# Revit family: Emergency_Equipment-Haws_Corporation-Laboratory_Combination_Unit_8356WCC new
name_source: partatom
category: Plumbing Fixtures
revit_build: Autodesk Revit Architecture 2015 (Build: 20160512_1515(x64)
units: mm (PartAtom-declared; Revit-internal decimal feet)

## types (1)
- 8356WCC
    Assembly Code = D2010710
    CW Connection = Yes
    CWFU = 1
    Cabinet = Metal - Haws Corporation - Polished Chrome
    Ceiling Level = 8' - 0"
    Cost = 0 $
    Cost Note = For Cost information please visit the Resource tab in the Product Page URL
    Default Elevation = 1' - 9 7/8"
    Description = Emergency combination unit is equipped with a stainless steel drain pan
    Flow = 20 GPM
    HW Connection = No
    HWFU = 1
    Keynote = 15410
    Manufacturer = Haws Corporation
    Model = 8356WCC
    Product Documentation Link = https://www.hawsco.com
    Product Page URL = http://www.hawsco.com
    Pull Down Lever = 2' - 10 1/2"
    Pull Lever = Metal - Haws Corporation - Smokey Pearl
    Sanitary Radius = 0' - 0 3/4"
    Series = Omni-Flo
    Shower Head = Metal - Haws Corporation - Green Powder Coating
    Supply Radius = 0' - 0 1/2"
    Thikness = 0' - 0 1/8"
    Tubing = Metal - Haws Corporation - Galvanized Steel
    Type Comments = Barrier-free eye/face Wash Combines
    URL = http://www.hawsco.com
    Vent Connection = No
    Version = 2014-v2.0a
    WFU = 1
    Waste Connection = Yes

## geometry (parser evidence)
native form markers: Blend x14, Sweep x14
no freeform markers — native parametric forms only
